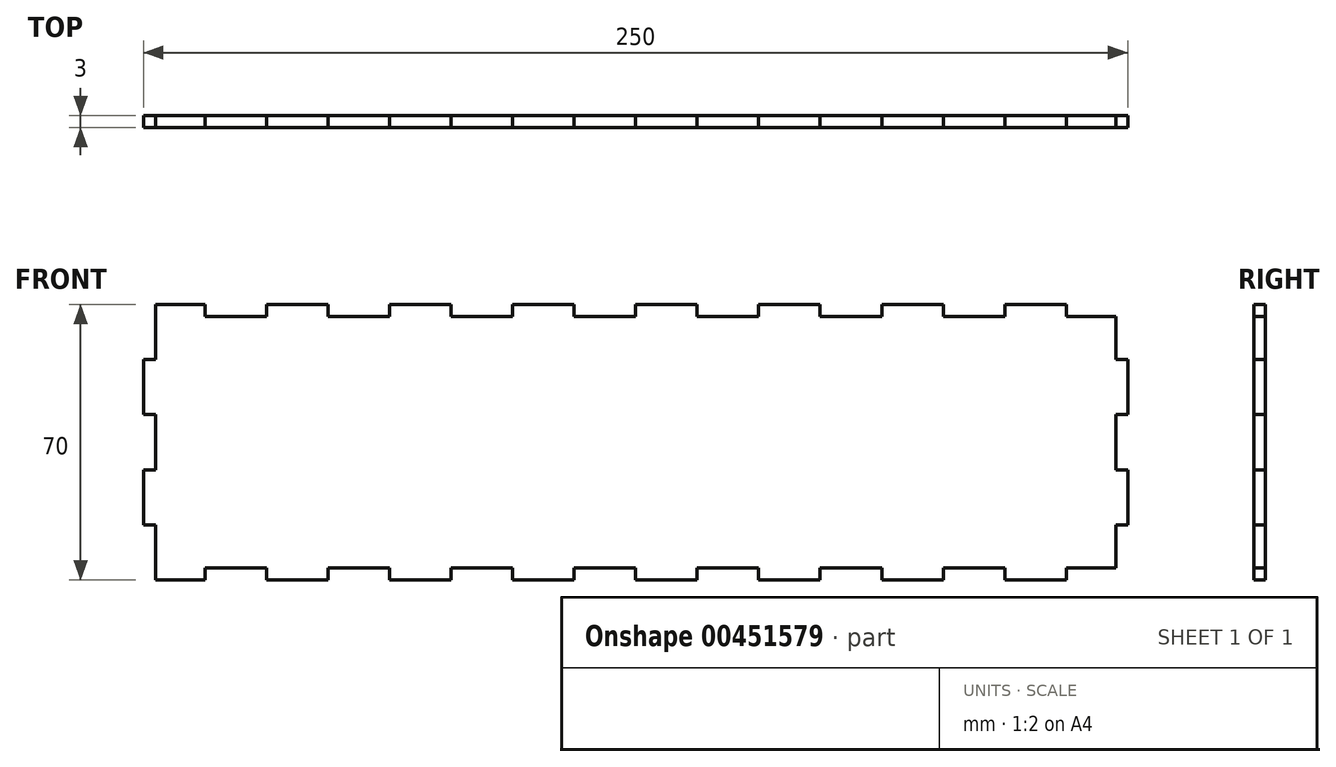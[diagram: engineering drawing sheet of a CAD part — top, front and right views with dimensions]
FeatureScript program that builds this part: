
annotation { "Feature Type Name" : "Feature", "Feature Type Description" : "" }
export const myFeature = defineFeature(function(context is Context, id is Id, definition is map)
    precondition{}
    {
        {
            var Q0;
            Q0=qCreatedBy(makeId("Front.planeOp"),FACE);
            var sketch = newSketch(context, id + "F0", { "sketchPlane" : qUnion([Q0])});
            skLineSegment(sketch, "E0.top", {"start": v(109.38, 35) * mm, "end": v(93.75, 35) * mm});
            skLineSegment(sketch, "E0.right", {"start": v(-125, -21) * mm, "end": v(-125, -7) * mm});
            skPoint(sketch, "E0.middle", {"position": v(0, 0) * mm});
            skLineSegment(sketch, "E1", {"start": v(-122, 35) * mm, "end": v(-122, 21) * mm});
            skLineSegment(sketch, "E2", {"start": v(-125, 21) * mm, "end": v(-122, 21) * mm});
            skLineSegment(sketch, "E3", {"start": v(-125, 7) * mm, "end": v(-122, 7) * mm});
            skLineSegment(sketch, "E4", {"start": v(-125, -7) * mm, "end": v(-122, -7) * mm});
            skLineSegment(sketch, "E5", {"start": v(-125, -21) * mm, "end": v(-122, -21) * mm});
            skPoint(sketch, "E6.orphan", {"position": v(-125, 35) * mm});
            skLineSegment(sketch, "E7.trimOffspring", {"start": v(-122, 7) * mm, "end": v(-122, -7) * mm});
            skLineSegment(sketch, "E8.trimOffspring", {"start": v(-125, 7) * mm, "end": v(-125, 21) * mm});
            skLineSegment(sketch, "E9.trimOffspring", {"start": v(-122, -21) * mm, "end": v(-122, -35) * mm});
            skPoint(sketch, "E10.orphan", {"position": v(-125, -35) * mm});
            skLineSegment(sketch, "E11.MirrorCS", {"start": v(125, -7) * mm, "end": v(122, -7) * mm});
            skLineSegment(sketch, "E12.MirrorCS", {"start": v(125, -21) * mm, "end": v(122, -21) * mm});
            skLineSegment(sketch, "E13.MirrorCS", {"start": v(122, 7) * mm, "end": v(122, -7) * mm});
            skLineSegment(sketch, "E14.MirrorCS", {"start": v(-122, 35) * mm, "end": v(-109.38, 35) * mm});
            skLineSegment(sketch, "E15.MirrorCS", {"start": v(125, -21) * mm, "end": v(125, -7) * mm});
            skLineSegment(sketch, "E16.MirrorCS", {"start": v(125, 7) * mm, "end": v(125, 21) * mm});
            skLineSegment(sketch, "E17.MirrorCS", {"start": v(125, 7) * mm, "end": v(122, 7) * mm});
            skLineSegment(sketch, "E18.MirrorCS", {"start": v(122, -21) * mm, "end": v(122, -32) * mm});
            skPoint(sketch, "E19.MirrorP", {"position": v(125, -35) * mm});
            skLineSegment(sketch, "E20.MirrorCS", {"start": v(122, 32) * mm, "end": v(122, 21) * mm});
            skPoint(sketch, "E21.MirrorP", {"position": v(125, 35) * mm});
            skLineSegment(sketch, "E22.MirrorCS", {"start": v(125, 21) * mm, "end": v(122, 21) * mm});
            skLineSegment(sketch, "E23", {"start": v(-109.38, 32) * mm, "end": v(-93.75, 32) * mm});
            skLineSegment(sketch, "E24", {"start": v(-109.38, 35) * mm, "end": v(-109.38, 32) * mm});
            skLineSegment(sketch, "E25", {"start": v(-93.75, 35) * mm, "end": v(-93.75, 32) * mm});
            skLineSegment(sketch, "E26", {"start": v(-78.12, 35) * mm, "end": v(-78.12, 32) * mm});
            skLineSegment(sketch, "E27", {"start": v(-62.5, 35) * mm, "end": v(-62.5, 32) * mm});
            skLineSegment(sketch, "E28", {"start": v(-46.88, 35) * mm, "end": v(-46.88, 32) * mm});
            skLineSegment(sketch, "E29", {"start": v(-31.25, 35) * mm, "end": v(-31.25, 32) * mm});
            skLineSegment(sketch, "E30", {"start": v(-15.62, 35) * mm, "end": v(-15.62, 32) * mm});
            skLineSegment(sketch, "E31", {"start": v(0, 35) * mm, "end": v(0, 32) * mm});
            skLineSegment(sketch, "E32.MirrorCS", {"start": v(93.75, 35) * mm, "end": v(93.75, 32) * mm});
            skLineSegment(sketch, "E33.MirrorCS", {"start": v(78.12, 35) * mm, "end": v(78.12, 32) * mm});
            skLineSegment(sketch, "E34.MirrorCS", {"start": v(62.5, 35) * mm, "end": v(62.5, 32) * mm});
            skLineSegment(sketch, "E35.MirrorCS", {"start": v(31.25, 35) * mm, "end": v(31.25, 32) * mm});
            skLineSegment(sketch, "E36.MirrorCS", {"start": v(109.38, 35) * mm, "end": v(109.38, 32) * mm});
            skLineSegment(sketch, "E37.MirrorCS", {"start": v(46.88, 35) * mm, "end": v(46.88, 32) * mm});
            skLineSegment(sketch, "E38.MirrorCS", {"start": v(15.62, 35) * mm, "end": v(15.62, 32) * mm});
            skLineSegment(sketch, "E39.MirrorCS", {"start": v(0, -35) * mm, "end": v(0, -32) * mm});
            skLineSegment(sketch, "E40.MirrorCS", {"start": v(-31.25, -35) * mm, "end": v(-31.25, -32) * mm});
            skLineSegment(sketch, "E41.MirrorCS", {"start": v(15.62, -35) * mm, "end": v(15.62, -32) * mm});
            skLineSegment(sketch, "E42.MirrorCS", {"start": v(93.75, -35) * mm, "end": v(93.75, -32) * mm});
            skLineSegment(sketch, "E43.MirrorCS", {"start": v(31.25, -35) * mm, "end": v(31.25, -32) * mm});
            skLineSegment(sketch, "E44.MirrorCS", {"start": v(-46.88, -35) * mm, "end": v(-46.88, -32) * mm});
            skLineSegment(sketch, "E45.MirrorCS", {"start": v(-122, -35) * mm, "end": v(-109.38, -35) * mm});
            skLineSegment(sketch, "E46.MirrorCS", {"start": v(109.38, -35) * mm, "end": v(109.38, -32) * mm});
            skLineSegment(sketch, "E47.MirrorCS", {"start": v(-62.5, -35) * mm, "end": v(-62.5, -32) * mm});
            skLineSegment(sketch, "E48.MirrorCS", {"start": v(-109.38, -35) * mm, "end": v(-109.38, -32) * mm});
            skLineSegment(sketch, "E49.MirrorCS", {"start": v(-78.12, -35) * mm, "end": v(-78.12, -32) * mm});
            skLineSegment(sketch, "E50.MirrorCS", {"start": v(-15.62, -35) * mm, "end": v(-15.62, -32) * mm});
            skLineSegment(sketch, "E51.MirrorCS", {"start": v(46.88, -35) * mm, "end": v(46.88, -32) * mm});
            skLineSegment(sketch, "E52.MirrorCS", {"start": v(62.5, -35) * mm, "end": v(62.5, -32) * mm});
            skLineSegment(sketch, "E53.MirrorCS", {"start": v(78.12, -35) * mm, "end": v(78.12, -32) * mm});
            skLineSegment(sketch, "E54.MirrorCS", {"start": v(-93.75, -35) * mm, "end": v(-93.75, -32) * mm});
            skLineSegment(sketch, "E55.MirrorCS", {"start": v(-109.38, -32) * mm, "end": v(-93.75, -32) * mm});
            skPoint(sketch, "E56.orphan", {"position": v(-122, 32) * mm});
            skLineSegment(sketch, "E57.trimOffspring", {"start": v(-109.38, 35) * mm, "end": v(-122, 35) * mm});
            skLineSegment(sketch, "E58.trimOffspring", {"start": v(-93.75, 35) * mm, "end": v(-78.12, 35) * mm});
            skLineSegment(sketch, "E59.trimOffspring", {"start": v(-78.12, 32) * mm, "end": v(-62.5, 32) * mm});
            skLineSegment(sketch, "E60.trimOffspring", {"start": v(-62.5, 35) * mm, "end": v(-46.88, 35) * mm});
            skLineSegment(sketch, "E61.trimOffspring", {"start": v(-78.12, 35) * mm, "end": v(-93.75, 35) * mm});
            skLineSegment(sketch, "E62.trimOffspring", {"start": v(-46.88, 32) * mm, "end": v(-31.25, 32) * mm});
            skLineSegment(sketch, "E63.trimOffspring", {"start": v(-46.88, 35) * mm, "end": v(-62.5, 35) * mm});
            skLineSegment(sketch, "E64.trimOffspring", {"start": v(-31.25, 35) * mm, "end": v(-15.62, 35) * mm});
            skLineSegment(sketch, "E65.trimOffspring", {"start": v(-15.62, 32) * mm, "end": v(0, 32) * mm});
            skLineSegment(sketch, "E66.trimOffspring", {"start": v(-15.62, 35) * mm, "end": v(-31.25, 35) * mm});
            skLineSegment(sketch, "E67.trimOffspring", {"start": v(0, 35) * mm, "end": v(15.62, 35) * mm});
            skLineSegment(sketch, "E68.trimOffspring", {"start": v(15.62, 32) * mm, "end": v(31.25, 32) * mm});
            skLineSegment(sketch, "E69.trimOffspring", {"start": v(31.25, 35) * mm, "end": v(46.88, 35) * mm});
            skLineSegment(sketch, "E70.trimOffspring", {"start": v(15.62, 35) * mm, "end": v(0, 35) * mm});
            skLineSegment(sketch, "E71.trimOffspring", {"start": v(46.88, 32) * mm, "end": v(62.5, 32) * mm});
            skLineSegment(sketch, "E72.trimOffspring", {"start": v(46.88, 35) * mm, "end": v(31.25, 35) * mm});
            skLineSegment(sketch, "E73.trimOffspring", {"start": v(62.5, 35) * mm, "end": v(78.12, 35) * mm});
            skLineSegment(sketch, "E74.trimOffspring", {"start": v(78.12, 32) * mm, "end": v(93.75, 32) * mm});
            skLineSegment(sketch, "E75.trimOffspring", {"start": v(93.75, 35) * mm, "end": v(109.38, 35) * mm});
            skLineSegment(sketch, "E76.trimOffspring", {"start": v(78.12, 35) * mm, "end": v(62.5, 35) * mm});
            skLineSegment(sketch, "E77.trimOffspring", {"start": v(109.38, 32) * mm, "end": v(122, 32) * mm});
            skPoint(sketch, "E78.orphan", {"position": v(122, 35) * mm});
            skPoint(sketch, "E79.orphan", {"position": v(-122, -32) * mm});
            skLineSegment(sketch, "E80.trimOffspring", {"start": v(-109.38, -35) * mm, "end": v(-122, -35) * mm});
            skLineSegment(sketch, "E81.trimOffspring", {"start": v(-93.75, -35) * mm, "end": v(-78.12, -35) * mm});
            skLineSegment(sketch, "E82.trimOffspring", {"start": v(-78.12, -32) * mm, "end": v(-62.5, -32) * mm});
            skLineSegment(sketch, "E83.trimOffspring", {"start": v(-78.12, -35) * mm, "end": v(-93.75, -35) * mm});
            skLineSegment(sketch, "E84.trimOffspring", {"start": v(-62.5, -35) * mm, "end": v(-46.88, -35) * mm});
            skLineSegment(sketch, "E85.trimOffspring", {"start": v(-46.88, -32) * mm, "end": v(-31.25, -32) * mm});
            skLineSegment(sketch, "E86.trimOffspring", {"start": v(-31.25, -35) * mm, "end": v(-15.62, -35) * mm});
            skLineSegment(sketch, "E87.trimOffspring", {"start": v(-46.88, -35) * mm, "end": v(-62.5, -35) * mm});
            skLineSegment(sketch, "E88.trimOffspring", {"start": v(-15.62, -32) * mm, "end": v(0, -32) * mm});
            skLineSegment(sketch, "E89.trimOffspring", {"start": v(-15.62, -35) * mm, "end": v(-31.25, -35) * mm});
            skLineSegment(sketch, "E90.trimOffspring", {"start": v(0, -35) * mm, "end": v(15.62, -35) * mm});
            skLineSegment(sketch, "E91.trimOffspring", {"start": v(15.62, -32) * mm, "end": v(31.25, -32) * mm});
            skLineSegment(sketch, "E92.trimOffspring", {"start": v(15.62, -35) * mm, "end": v(0, -35) * mm});
            skLineSegment(sketch, "E93.trimOffspring", {"start": v(46.88, -32) * mm, "end": v(62.5, -32) * mm});
            skLineSegment(sketch, "E94.trimOffspring", {"start": v(62.5, -35) * mm, "end": v(78.12, -35) * mm});
            skLineSegment(sketch, "E95.trimOffspring", {"start": v(46.88, -35) * mm, "end": v(31.25, -35) * mm});
            skLineSegment(sketch, "E96.trimOffspring", {"start": v(78.12, -32) * mm, "end": v(93.75, -32) * mm});
            skLineSegment(sketch, "E97.trimOffspring", {"start": v(78.12, -35) * mm, "end": v(62.5, -35) * mm});
            skLineSegment(sketch, "E98.trimOffspring", {"start": v(93.75, -35) * mm, "end": v(109.38, -35) * mm});
            skLineSegment(sketch, "E99.trimOffspring", {"start": v(109.38, -32) * mm, "end": v(122, -32) * mm});
            skPoint(sketch, "E100.orphan", {"position": v(122, -35) * mm});
            skSolve(sketch);
        }
        {
            var Q0;
            Q0=makeQuery(id+"F0.imprint","IMPRINT",FACE,{"disambiguationData":[TD([[makeQuery(id+"F0.imprint","IMPRINT",EDGE,{"derivedFrom":sQuery(id+"F0.wireOp",EDGE,"E0.right")}),-1.0]])]});
            extrude(context, id + "F1", {"entities" : qUnion([Q0]), "depth" : 3 * mm, "offsetDistance" : 25 * mm});
        }
    });
